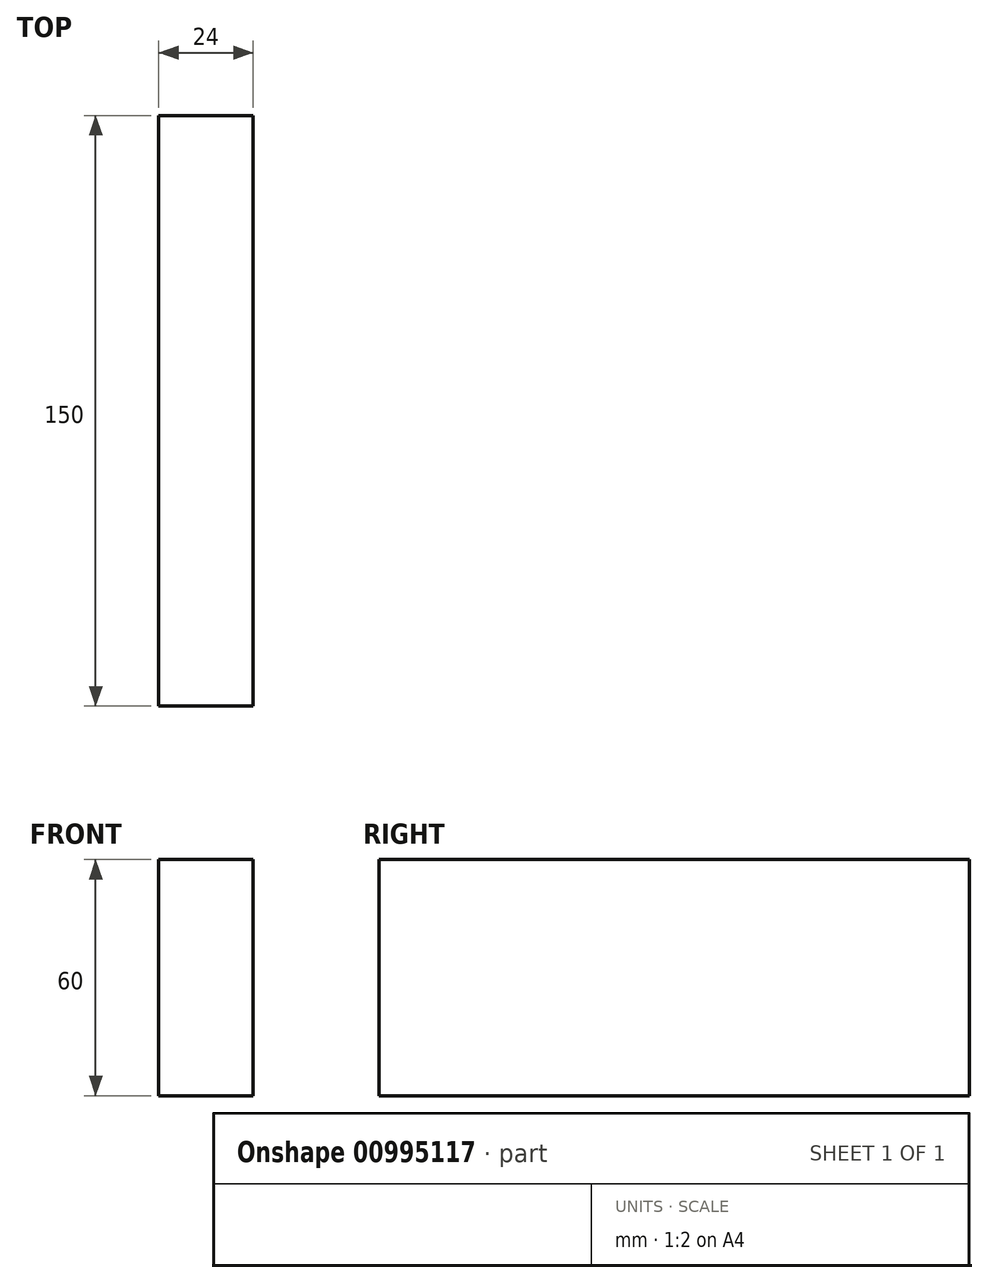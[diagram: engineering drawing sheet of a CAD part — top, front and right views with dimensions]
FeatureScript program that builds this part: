
annotation { "Feature Type Name" : "Feature", "Feature Type Description" : "" }
export const myFeature = defineFeature(function(context is Context, id is Id, definition is map)
    precondition{}
    {
        {
            var Q0;
            Q0=qCreatedBy(makeId("Front.planeOp"),FACE);
            var sketch = newSketch(context, id + "F0", { "sketchPlane" : qUnion([Q0])});
            skLineSegment(sketch, "E0.bottom", {"start": v(0, 0) * mm, "end": v(24, 0) * mm});
            skLineSegment(sketch, "E0.top", {"start": v(0, 60) * mm, "end": v(24, 60) * mm});
            skLineSegment(sketch, "E0.left", {"start": v(0, 0) * mm, "end": v(0, 60) * mm});
            skLineSegment(sketch, "E0.right", {"start": v(24, 0) * mm, "end": v(24, 60) * mm});
            skSolve(sketch);
        }
        {
            var Q0;
            Q0 = qSketchRegion(id + "F0", true);
            extrude(context, id + "F1", {"entities" : qUnion([Q0]), "oppositeDirection" : true, "depth" : 150 * mm, "offsetDistance" : 25 * mm});
        }
    });
